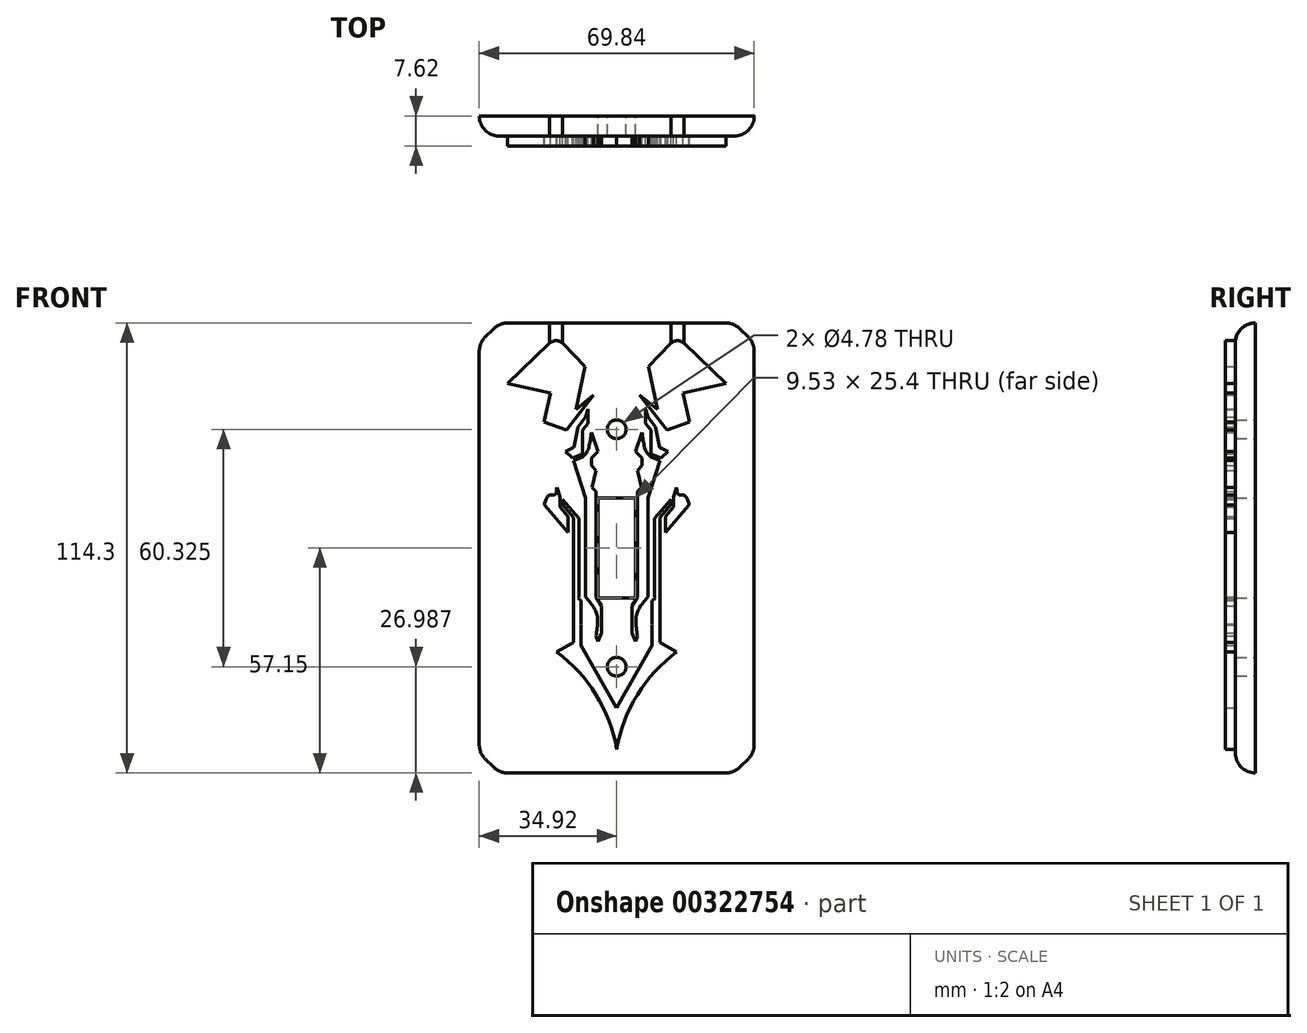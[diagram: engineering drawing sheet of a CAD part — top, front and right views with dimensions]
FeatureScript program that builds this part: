
annotation { "Feature Type Name" : "Feature", "Feature Type Description" : "" }
export const myFeature = defineFeature(function(context is Context, id is Id, definition is map)
    precondition{}
    {
        {
            var Q0;
            Q0=qCreatedBy(makeId("Front.planeOp"),FACE);
            var sketch = newSketch(context, id + "F0", { "sketchPlane" : qUnion([Q0])});
            skLineSegment(sketch, "E0.bottom", {"start": v(34.92, 57.15) * mm, "end": v(-34.93, 57.15) * mm});
            skLineSegment(sketch, "E0.top", {"start": v(34.93, -57.15) * mm, "end": v(-34.92, -57.15) * mm});
            skLineSegment(sketch, "E0.left", {"start": v(34.92, 57.15) * mm, "end": v(34.93, -57.15) * mm});
            skLineSegment(sketch, "E0.right", {"start": v(-34.93, 57.15) * mm, "end": v(-34.92, -57.15) * mm});
            skPoint(sketch, "E0.middle", {"position": v(0, 0) * mm});
            skCircle(sketch, "E1", {"center": v(0, 30.16) * mm, "radius": 2.39 * mm});
            skCircle(sketch, "E2", {"center": v(0, -30.16) * mm, "radius": 2.39 * mm});
            skLineSegment(sketch, "E3.bottom", {"start": v(4.76, -12.7) * mm, "end": v(-4.76, -12.7) * mm});
            skLineSegment(sketch, "E3.top", {"start": v(4.76, 12.7) * mm, "end": v(-4.76, 12.7) * mm});
            skLineSegment(sketch, "E3.left", {"start": v(4.76, -12.7) * mm, "end": v(4.76, 12.7) * mm});
            skLineSegment(sketch, "E3.right", {"start": v(-4.76, -12.7) * mm, "end": v(-4.76, 12.7) * mm});
            skSolve(sketch);
        }
        {
            var Q0;
            Q0 = qSketchRegion(id + "F0", true);
            extrude(context, id + "F1", {"entities" : qUnion([Q0]), "depth" : 5.08 * mm});
        }
        {
            var Q0;
            Q0=makeQuery(id+"F1.opExtrude","SWEPT_EDGE",EDGE,{"disambiguationData":[OSD([sQuery(id+"F0.wireOp",EDGE,"E0.top"),sQuery(id+"F0.wireOp",EDGE,"E0.right")])]});
            var Q1;
            Q1=makeQuery(id+"F1.opExtrude","SWEPT_EDGE",EDGE,{"disambiguationData":[OSD([sQuery(id+"F0.wireOp",EDGE,"E0.top"),sQuery(id+"F0.wireOp",EDGE,"E0.left")])]});
            var Q2;
            Q2=makeQuery(id+"F1.opExtrude","SWEPT_EDGE",EDGE,{"disambiguationData":[OSD([sQuery(id+"F0.wireOp",EDGE,"E0.bottom"),sQuery(id+"F0.wireOp",EDGE,"E0.left")])]});
            var Q3;
            Q3=makeQuery(id+"F1.opExtrude","SWEPT_EDGE",EDGE,{"disambiguationData":[OSD([sQuery(id+"F0.wireOp",EDGE,"E0.bottom"),sQuery(id+"F0.wireOp",EDGE,"E0.right")])]});
            chamfer(context, id + "F2", {"entities" : qUnion([Q0, Q1, Q2, Q3]), "width" : 5.08 * mm, "tangentPropagation" : true});
        }
        {
            var Q0;
            Q0=makeQuery(id+"F1.opExtrude","CAP_FACE",FACE,{"disambiguationData":[OSD([sQuery(id+"F0.wireOp",EDGE,"E0.bottom"),sQuery(id+"F0.wireOp",EDGE,"E0.top"),sQuery(id+"F0.wireOp",EDGE,"E0.left"),sQuery(id+"F0.wireOp",EDGE,"E0.right"),sQuery(id+"F0.wireOp",EDGE,"E1"),sQuery(id+"F0.wireOp",EDGE,"E2"),sQuery(id+"F0.wireOp",EDGE,"E3.bottom"),sQuery(id+"F0.wireOp",EDGE,"E3.top"),sQuery(id+"F0.wireOp",EDGE,"E3.left"),sQuery(id+"F0.wireOp",EDGE,"E3.right")])],"isStart":false});
            var sketch = newSketch(context, id + "F3", { "sketchPlane" : qUnion([Q0])});
            skLineSegment(sketch, "E4", {"start": v(-15.24, -26.4) * mm, "end": v(-10.95, -24.02) * mm});
            skLineSegment(sketch, "E5", {"start": v(15.24, -26.4) * mm, "end": v(10.95, -24.02) * mm});
            skArc(sketch, "E6", {"start": v(0, -51.12) * mm, "mid": v(-5.25, -37.3) * mm, "end": v(-15.24, -26.4) * mm});
            skLineSegment(sketch, "E7", {"start": v(-10.95, -24.02) * mm, "end": v(-10.95, 7.77) * mm});
            skLineSegment(sketch, "E8", {"start": v(-10.95, 7.77) * mm, "end": v(-13.78, 11.03) * mm});
            skLineSegment(sketch, "E9", {"start": v(-13.78, 11.03) * mm, "end": v(-13.78, 12.37) * mm});
            skLineSegment(sketch, "E10", {"start": v(-13.78, 12.37) * mm, "end": v(-9.6, 7.55) * mm});
            skLineSegment(sketch, "E11", {"start": v(-9.6, 7.55) * mm, "end": v(-9.6, -12.48) * mm});
            skLineSegment(sketch, "E12", {"start": v(-9.6, -12.48) * mm, "end": v(-9.83, -12.8) * mm});
            skArc(sketch, "E13.MirrorCS", {"start": v(0, -51.12) * mm, "mid": v(5.25, -37.3) * mm, "end": v(15.24, -26.4) * mm});
            skLineSegment(sketch, "E14", {"start": v(-9.83, -12.8) * mm, "end": v(-9.02, -13.37) * mm});
            skLineSegment(sketch, "E15", {"start": v(-9.02, -13.37) * mm, "end": v(-9.02, -19.24) * mm});
            skLineSegment(sketch, "E16", {"start": v(-9.02, -19.24) * mm, "end": v(-9.2, -19.37) * mm});
            skLineSegment(sketch, "E17", {"start": v(-9.2, -19.37) * mm, "end": v(-9.02, -19.6) * mm});
            skLineSegment(sketch, "E18", {"start": v(-9.02, -19.6) * mm, "end": v(-9.02, -24.8) * mm});
            skLineSegment(sketch, "E19", {"start": v(9.02, -24.8) * mm, "end": v(0, -40.68) * mm});
            skLineSegment(sketch, "E20", {"start": v(0, -40.68) * mm, "end": v(-9.02, -24.8) * mm});
            skLineSegment(sketch, "E21.MirrorCS", {"start": v(9.6, 7.55) * mm, "end": v(9.6, -12.48) * mm});
            skLineSegment(sketch, "E22.MirrorCS", {"start": v(10.95, -24.02) * mm, "end": v(10.95, 7.77) * mm});
            skLineSegment(sketch, "E23.MirrorCS", {"start": v(9.6, -12.48) * mm, "end": v(9.83, -12.8) * mm});
            skLineSegment(sketch, "E24.MirrorCS", {"start": v(9.83, -12.8) * mm, "end": v(9.02, -13.37) * mm});
            skLineSegment(sketch, "E25.MirrorCS", {"start": v(9.02, -19.6) * mm, "end": v(9.02, -24.8) * mm});
            skLineSegment(sketch, "E26.MirrorCS", {"start": v(9.02, -13.37) * mm, "end": v(9.02, -19.24) * mm});
            skLineSegment(sketch, "E27.MirrorCS", {"start": v(9.02, -19.24) * mm, "end": v(9.2, -19.37) * mm});
            skLineSegment(sketch, "E28.MirrorCS", {"start": v(9.2, -19.37) * mm, "end": v(9.02, -19.6) * mm});
            skLineSegment(sketch, "E29.MirrorCS", {"start": v(13.78, 12.37) * mm, "end": v(9.6, 7.55) * mm});
            skLineSegment(sketch, "E30.MirrorCS", {"start": v(10.95, 7.77) * mm, "end": v(13.78, 11.03) * mm});
            skLineSegment(sketch, "E31.MirrorCS", {"start": v(13.78, 11.03) * mm, "end": v(13.78, 12.37) * mm});
            skPoint(sketch, "E32.trimOffspring.end.orphan", {"position": v(0, -57.15) * mm});
            skLineSegment(sketch, "E33", {"start": v(14.43, 12.95) * mm, "end": v(14.43, 10.37) * mm});
            skLineSegment(sketch, "E34", {"start": v(14.43, 10.37) * mm, "end": v(12.35, 7.97) * mm});
            skLineSegment(sketch, "E35", {"start": v(12.35, 7.97) * mm, "end": v(12.35, 3.96) * mm});
            skLineSegment(sketch, "E36", {"start": v(12.35, 3.96) * mm, "end": v(18.4, 10.94) * mm});
            skFitSpline(sketch, "E37", {"points": [v(18.4, 10.94) * mm, v(17.22, 13.37) * mm, v(15.73, 13.58) * mm, v(15.22, 15.38) * mm], "startDerivative": vector(-2.14, 8.3) * mm, "endDerivative": vector(-0.48, 7.26) * mm});
            skLineSegment(sketch, "E38.MirrorCS", {"start": v(-12.35, 7.97) * mm, "end": v(-12.35, 3.96) * mm});
            skLineSegment(sketch, "E39.MirrorCS", {"start": v(-12.35, 3.96) * mm, "end": v(-18.4, 10.94) * mm});
            skFitSpline(sketch, "E40.MirrorCS", {"points": [v(-18.4, 10.94) * mm, v(-17.22, 13.37) * mm, v(-15.73, 13.58) * mm, v(-15.22, 15.38) * mm], "startDerivative": vector(2.14, 8.3) * mm, "endDerivative": vector(0.48, 7.26) * mm});
            skLineSegment(sketch, "E41.MirrorCS", {"start": v(-14.43, 12.95) * mm, "end": v(-14.43, 10.37) * mm});
            skLineSegment(sketch, "E42.MirrorCS", {"start": v(-14.43, 10.37) * mm, "end": v(-12.35, 7.97) * mm});
            skLineSegment(sketch, "E43", {"start": v(15.22, 15.38) * mm, "end": v(14.43, 12.95) * mm});
            skLineSegment(sketch, "E44", {"start": v(-15.22, 15.38) * mm, "end": v(-14.43, 12.95) * mm});
            skFitSpline(sketch, "E45", {"points": [v(-7.9, -12.48) * mm, v(-5.07, -16.74) * mm, v(-5.28, -22.34) * mm], "startDerivative": vector(7.33, -8.17) * mm, "endDerivative": vector(-2.02, -11.52) * mm});
            skLineSegment(sketch, "E46", {"start": v(-5.28, -22.34) * mm, "end": v(-4.76, -23.8) * mm});
            skLineSegment(sketch, "E47", {"start": v(-4.76, -23.8) * mm, "end": v(-3.9, -21.54) * mm});
            skLineSegment(sketch, "E48", {"start": v(-3.9, -21.54) * mm, "end": v(-3.9, -14.77) * mm});
            skLineSegment(sketch, "E49", {"start": v(-3.9, -14.77) * mm, "end": v(-5.28, -12.48) * mm});
            skLineSegment(sketch, "E50", {"start": v(-5.28, -12.48) * mm, "end": v(-5.28, 14.37) * mm});
            skLineSegment(sketch, "E51", {"start": v(-5.28, 14.37) * mm, "end": v(-6.27, 15.34) * mm});
            skLineSegment(sketch, "E52", {"start": v(-6.27, 15.34) * mm, "end": v(-5.28, 19.71) * mm});
            skLineSegment(sketch, "E53", {"start": v(-5.28, 19.71) * mm, "end": v(-6.46, 20.97) * mm});
            skLineSegment(sketch, "E54", {"start": v(-6.46, 20.97) * mm, "end": v(-6.46, 22.92) * mm});
            skLineSegment(sketch, "E55", {"start": v(-6.46, 22.92) * mm, "end": v(-4.76, 24.47) * mm});
            skLineSegment(sketch, "E56", {"start": v(-4.76, 24.47) * mm, "end": v(-6.46, 29.33) * mm});
            skFitSpline(sketch, "E57", {"points": [v(-6.46, 29.33) * mm, v(-7.9, 23.89) * mm, v(-10.95, 22.24) * mm], "startDerivative": vector(-1.35, -11.37) * mm, "endDerivative": vector(-7.89, -2.45) * mm});
            skLineSegment(sketch, "E58", {"start": v(-10.95, 22.24) * mm, "end": v(-7.9, 12.72) * mm});
            skLineSegment(sketch, "E59", {"start": v(-7.9, 12.72) * mm, "end": v(-7.9, -12.48) * mm});
            skLineSegment(sketch, "E60.MirrorCS", {"start": v(5.28, 19.71) * mm, "end": v(6.46, 20.97) * mm});
            skLineSegment(sketch, "E61.MirrorCS", {"start": v(6.46, 20.97) * mm, "end": v(6.46, 22.92) * mm});
            skLineSegment(sketch, "E62.MirrorCS", {"start": v(6.46, 22.92) * mm, "end": v(4.76, 24.47) * mm});
            skLineSegment(sketch, "E63.MirrorCS", {"start": v(4.76, 24.47) * mm, "end": v(6.46, 29.33) * mm});
            skFitSpline(sketch, "E64.MirrorCS", {"points": [v(6.46, 29.33) * mm, v(7.9, 23.89) * mm, v(10.95, 22.24) * mm], "startDerivative": vector(1.35, -11.37) * mm, "endDerivative": vector(7.89, -2.45) * mm});
            skLineSegment(sketch, "E65.MirrorCS", {"start": v(10.95, 22.24) * mm, "end": v(7.9, 12.72) * mm});
            skLineSegment(sketch, "E66.MirrorCS", {"start": v(7.9, 12.72) * mm, "end": v(7.9, -12.48) * mm});
            skLineSegment(sketch, "E67.MirrorCS", {"start": v(5.28, -12.48) * mm, "end": v(5.28, 14.37) * mm});
            skLineSegment(sketch, "E68.MirrorCS", {"start": v(6.27, 15.34) * mm, "end": v(5.28, 19.71) * mm});
            skLineSegment(sketch, "E69.MirrorCS", {"start": v(5.28, 14.37) * mm, "end": v(6.27, 15.34) * mm});
            skFitSpline(sketch, "E70.MirrorCS", {"points": [v(7.9, -12.48) * mm, v(5.07, -16.74) * mm, v(5.28, -22.34) * mm], "startDerivative": vector(-7.33, -8.17) * mm, "endDerivative": vector(2.02, -11.52) * mm});
            skLineSegment(sketch, "E71.MirrorCS", {"start": v(3.9, -14.77) * mm, "end": v(5.28, -12.48) * mm});
            skLineSegment(sketch, "E72.MirrorCS", {"start": v(3.9, -21.54) * mm, "end": v(3.9, -14.77) * mm});
            skLineSegment(sketch, "E73.MirrorCS", {"start": v(4.76, -23.8) * mm, "end": v(3.9, -21.54) * mm});
            skLineSegment(sketch, "E74.MirrorCS", {"start": v(5.28, -22.34) * mm, "end": v(4.76, -23.8) * mm});
            skFitSpline(sketch, "E75.MirrorCS", {"points": [v(-6.46, 29.33) * mm, v(-7.9, 23.89) * mm, v(-10.95, 22.24) * mm], "startDerivative": vector(-1.35, -11.37) * mm, "endDerivative": vector(-7.89, -2.45) * mm});
            skLineSegment(sketch, "E76", {"start": v(11.28, 22.92) * mm, "end": v(13.05, 24.57) * mm});
            skLineSegment(sketch, "E77", {"start": v(13.05, 24.57) * mm, "end": v(11.2, 25.36) * mm});
            skLineSegment(sketch, "E78", {"start": v(10.9, 25.72) * mm, "end": v(9.8, 30.74) * mm});
            skLineSegment(sketch, "E79", {"start": v(9.8, 30.74) * mm, "end": v(7.9, 33.23) * mm});
            skLineSegment(sketch, "E80", {"start": v(7.9, 33.23) * mm, "end": v(7.25, 35.36) * mm});
            skLineSegment(sketch, "E81", {"start": v(7.25, 35.36) * mm, "end": v(7.25, 31.6) * mm});
            skLineSegment(sketch, "E82", {"start": v(7.25, 31.6) * mm, "end": v(8.66, 30) * mm});
            skLineSegment(sketch, "E83", {"start": v(8.66, 30) * mm, "end": v(8.66, 23.89) * mm});
            skLineSegment(sketch, "E84", {"start": v(8.66, 23.89) * mm, "end": v(11.28, 22.92) * mm});
            skPoint(sketch, "E85.visualSharp", {"position": v(10.95, 25.46) * mm});
            skArc(sketch, "E85.filletArc", {"start": v(10.9, 25.72) * mm, "mid": v(11, 25.5) * mm, "end": v(11.2, 25.36) * mm});
            skLineSegment(sketch, "E86.MirrorCS", {"start": v(-11.28, 22.92) * mm, "end": v(-13.05, 24.57) * mm});
            skLineSegment(sketch, "E87.MirrorCS", {"start": v(-8.66, 23.89) * mm, "end": v(-11.28, 22.92) * mm});
            skLineSegment(sketch, "E88.MirrorCS", {"start": v(-8.66, 30) * mm, "end": v(-8.66, 23.89) * mm});
            skLineSegment(sketch, "E89.MirrorCS", {"start": v(-13.05, 24.57) * mm, "end": v(-11.2, 25.36) * mm});
            skLineSegment(sketch, "E90.MirrorCS", {"start": v(-8.02, 25.67) * mm, "end": v(-6.92, 30.7) * mm});
            skArc(sketch, "E91.MirrorCS", {"start": v(-10.9, 25.72) * mm, "mid": v(-11, 25.5) * mm, "end": v(-11.2, 25.36) * mm});
            skLineSegment(sketch, "E92.MirrorCS", {"start": v(-9.8, 30.74) * mm, "end": v(-7.9, 33.23) * mm});
            skLineSegment(sketch, "E93.MirrorCS", {"start": v(-7.25, 35.36) * mm, "end": v(-7.25, 31.6) * mm});
            skLineSegment(sketch, "E94.MirrorCS", {"start": v(-7.9, 33.23) * mm, "end": v(-7.25, 35.36) * mm});
            skLineSegment(sketch, "E95.MirrorCS", {"start": v(-7.25, 31.6) * mm, "end": v(-8.66, 30) * mm});
            skPoint(sketch, "E96.trimOffspring.end.orphan", {"position": v(10.95, -24.02) * mm});
            skPoint(sketch, "E97.MirrorCS.start.orphan", {"position": v(-10.95, -24.02) * mm});
            skPoint(sketch, "E98.start.orphan", {"position": v(0, 57.15) * mm});
            skLineSegment(sketch, "E99", {"start": v(-12.73, 29.99) * mm, "end": v(-5.84, 38.83) * mm});
            skLineSegment(sketch, "E100", {"start": v(-5.84, 38.83) * mm, "end": v(-10.4, 35.23) * mm});
            skLineSegment(sketch, "E101", {"start": v(-10.4, 35.23) * mm, "end": v(-8.02, 46.11) * mm});
            skLineSegment(sketch, "E102", {"start": v(-8.02, 46.11) * mm, "end": v(-13.62, 51.9) * mm});
            skLineSegment(sketch, "E103", {"start": v(-17.22, 51.95) * mm, "end": v(-27.72, 41.77) * mm});
            skLineSegment(sketch, "E104", {"start": v(-27.72, 41.77) * mm, "end": v(-24.35, 41.03) * mm});
            skLineSegment(sketch, "E105", {"start": v(-24.35, 41.03) * mm, "end": v(-16.87, 39.39) * mm});
            skLineSegment(sketch, "E106", {"start": v(-16.87, 39.39) * mm, "end": v(-18.48, 32.06) * mm});
            skLineSegment(sketch, "E107", {"start": v(-18.48, 32.06) * mm, "end": v(-12.73, 29.99) * mm});
            skPoint(sketch, "E108.visualSharp", {"position": v(-15.4, 53.72) * mm});
            skArc(sketch, "E108.filletArc", {"start": v(-13.62, 51.9) * mm, "mid": v(-15.4, 52.67) * mm, "end": v(-17.22, 51.95) * mm});
            skLineSegment(sketch, "E109.MirrorCS", {"start": v(10.4, 35.23) * mm, "end": v(8.02, 46.11) * mm});
            skLineSegment(sketch, "E110.MirrorCS", {"start": v(5.84, 38.83) * mm, "end": v(10.4, 35.23) * mm});
            skLineSegment(sketch, "E111.MirrorCS", {"start": v(12.73, 29.99) * mm, "end": v(5.84, 38.83) * mm});
            skLineSegment(sketch, "E112.MirrorCS", {"start": v(18.48, 32.06) * mm, "end": v(12.73, 29.99) * mm});
            skLineSegment(sketch, "E113.MirrorCS", {"start": v(16.87, 39.39) * mm, "end": v(18.48, 32.06) * mm});
            skLineSegment(sketch, "E114.MirrorCS", {"start": v(24.35, 41.03) * mm, "end": v(16.87, 39.39) * mm});
            skLineSegment(sketch, "E115.MirrorCS", {"start": v(27.72, 41.77) * mm, "end": v(24.35, 41.03) * mm});
            skLineSegment(sketch, "E116.MirrorCS", {"start": v(17.22, 51.95) * mm, "end": v(27.72, 41.77) * mm});
            skArc(sketch, "E117.MirrorCS", {"start": v(13.62, 51.9) * mm, "mid": v(15.4, 52.67) * mm, "end": v(17.22, 51.95) * mm});
            skLineSegment(sketch, "E118.MirrorCS", {"start": v(8.02, 46.11) * mm, "end": v(13.62, 51.9) * mm});
            skLineSegment(sketch, "E119", {"start": v(-10.9, 25.72) * mm, "end": v(-9.8, 30.74) * mm});
            skSolve(sketch);
        }
        {
            var Q0;
            Q0 = qSketchRegion(id + "F3", true);
            extrude(context, id + "F4", {"entities" : qUnion([Q0]), "operationType" : NewBodyOperationType.ADD, "depth" : 2.54 * mm});
        }
        {
            var Q0;
            {var subQ0=sQuery(id+"F0.wireOp",EDGE,"E0.bottom");Q0=makeQuery(id+"F2.opChamfer","BLEND_EDGE",EDGE,{"blendedFrom":[makeQuery(id+"F1.opExtrude","SWEPT_EDGE",EDGE,{"disambiguationData":[OSD([subQ0,sQuery(id+"F0.wireOp",EDGE,"E0.left")])]}),makeQuery(id+"F1.opExtrude","SWEPT_FACE",FACE,{"disambiguationData":[OSD([subQ0])]})],"blendedInto":[makeQuery(id+"F1.opExtrude","SWEPT_FACE",FACE,{"disambiguationData":[OSD([subQ0])]})]});}
            var Q1;
            {var subQ0=sQuery(id+"F0.wireOp",EDGE,"E0.left");Q1=makeQuery(id+"F2.opChamfer","BLEND_EDGE",EDGE,{"blendedFrom":[makeQuery(id+"F1.opExtrude","SWEPT_EDGE",EDGE,{"disambiguationData":[OSD([sQuery(id+"F0.wireOp",EDGE,"E0.bottom"),subQ0])]}),makeQuery(id+"F1.opExtrude","SWEPT_FACE",FACE,{"disambiguationData":[OSD([subQ0])]})],"blendedInto":[makeQuery(id+"F1.opExtrude","SWEPT_FACE",FACE,{"disambiguationData":[OSD([subQ0])]})]});}
            var Q2;
            {var subQ0=sQuery(id+"F0.wireOp",EDGE,"E0.bottom");Q2=makeQuery(id+"F2.opChamfer","BLEND_EDGE",EDGE,{"blendedFrom":[makeQuery(id+"F1.opExtrude","SWEPT_EDGE",EDGE,{"disambiguationData":[OSD([subQ0,sQuery(id+"F0.wireOp",EDGE,"E0.right")])]}),makeQuery(id+"F1.opExtrude","SWEPT_FACE",FACE,{"disambiguationData":[OSD([subQ0])]})],"blendedInto":[makeQuery(id+"F1.opExtrude","SWEPT_FACE",FACE,{"disambiguationData":[OSD([subQ0])]})]});}
            var Q3;
            {var subQ0=sQuery(id+"F0.wireOp",EDGE,"E0.right");Q3=makeQuery(id+"F2.opChamfer","BLEND_EDGE",EDGE,{"blendedFrom":[makeQuery(id+"F1.opExtrude","SWEPT_EDGE",EDGE,{"disambiguationData":[OSD([sQuery(id+"F0.wireOp",EDGE,"E0.bottom"),subQ0])]}),makeQuery(id+"F1.opExtrude","SWEPT_FACE",FACE,{"disambiguationData":[OSD([subQ0])]})],"blendedInto":[makeQuery(id+"F1.opExtrude","SWEPT_FACE",FACE,{"disambiguationData":[OSD([subQ0])]})]});}
            var Q4;
            {var subQ0=sQuery(id+"F0.wireOp",EDGE,"E0.right");Q4=makeQuery(id+"F2.opChamfer","BLEND_EDGE",EDGE,{"blendedFrom":[makeQuery(id+"F1.opExtrude","SWEPT_EDGE",EDGE,{"disambiguationData":[OSD([sQuery(id+"F0.wireOp",EDGE,"E0.top"),subQ0])]}),makeQuery(id+"F1.opExtrude","SWEPT_FACE",FACE,{"disambiguationData":[OSD([subQ0])]})],"blendedInto":[makeQuery(id+"F1.opExtrude","SWEPT_FACE",FACE,{"disambiguationData":[OSD([subQ0])]})]});}
            var Q5;
            {var subQ0=sQuery(id+"F0.wireOp",EDGE,"E0.top");Q5=makeQuery(id+"F2.opChamfer","BLEND_EDGE",EDGE,{"blendedFrom":[makeQuery(id+"F1.opExtrude","SWEPT_EDGE",EDGE,{"disambiguationData":[OSD([subQ0,sQuery(id+"F0.wireOp",EDGE,"E0.right")])]}),makeQuery(id+"F1.opExtrude","SWEPT_FACE",FACE,{"disambiguationData":[OSD([subQ0])]})],"blendedInto":[makeQuery(id+"F1.opExtrude","SWEPT_FACE",FACE,{"disambiguationData":[OSD([subQ0])]})]});}
            var Q6;
            {var subQ0=sQuery(id+"F0.wireOp",EDGE,"E0.top");Q6=makeQuery(id+"F2.opChamfer","BLEND_EDGE",EDGE,{"blendedFrom":[makeQuery(id+"F1.opExtrude","SWEPT_EDGE",EDGE,{"disambiguationData":[OSD([subQ0,sQuery(id+"F0.wireOp",EDGE,"E0.left")])]}),makeQuery(id+"F1.opExtrude","SWEPT_FACE",FACE,{"disambiguationData":[OSD([subQ0])]})],"blendedInto":[makeQuery(id+"F1.opExtrude","SWEPT_FACE",FACE,{"disambiguationData":[OSD([subQ0])]})]});}
            var Q7;
            {var subQ0=sQuery(id+"F0.wireOp",EDGE,"E0.left");Q7=makeQuery(id+"F2.opChamfer","BLEND_EDGE",EDGE,{"blendedFrom":[makeQuery(id+"F1.opExtrude","SWEPT_EDGE",EDGE,{"disambiguationData":[OSD([sQuery(id+"F0.wireOp",EDGE,"E0.top"),subQ0])]}),makeQuery(id+"F1.opExtrude","SWEPT_FACE",FACE,{"disambiguationData":[OSD([subQ0])]})],"blendedInto":[makeQuery(id+"F1.opExtrude","SWEPT_FACE",FACE,{"disambiguationData":[OSD([subQ0])]})]});}
            fillet(context, id + "F5", {"entities" : qUnion([Q0, Q1, Q2, Q3, Q4, Q5, Q6, Q7]), "radius" : 5.08 * mm, "tangentPropagation" : true, "allowEdgeOverflow" : false});
        }
        {
            var Q0;
            Q0=makeQuery(id+"F1.opExtrude","CAP_EDGE",EDGE,{"disambiguationData":[OSD([sQuery(id+"F0.wireOp",EDGE,"E0.left")])],"isStart":false});
            fillet(context, id + "F6", {"entities" : qUnion([Q0]), "radius" : 5.08 * mm, "tangentPropagation" : true, "allowEdgeOverflow" : false});
        }
    });
